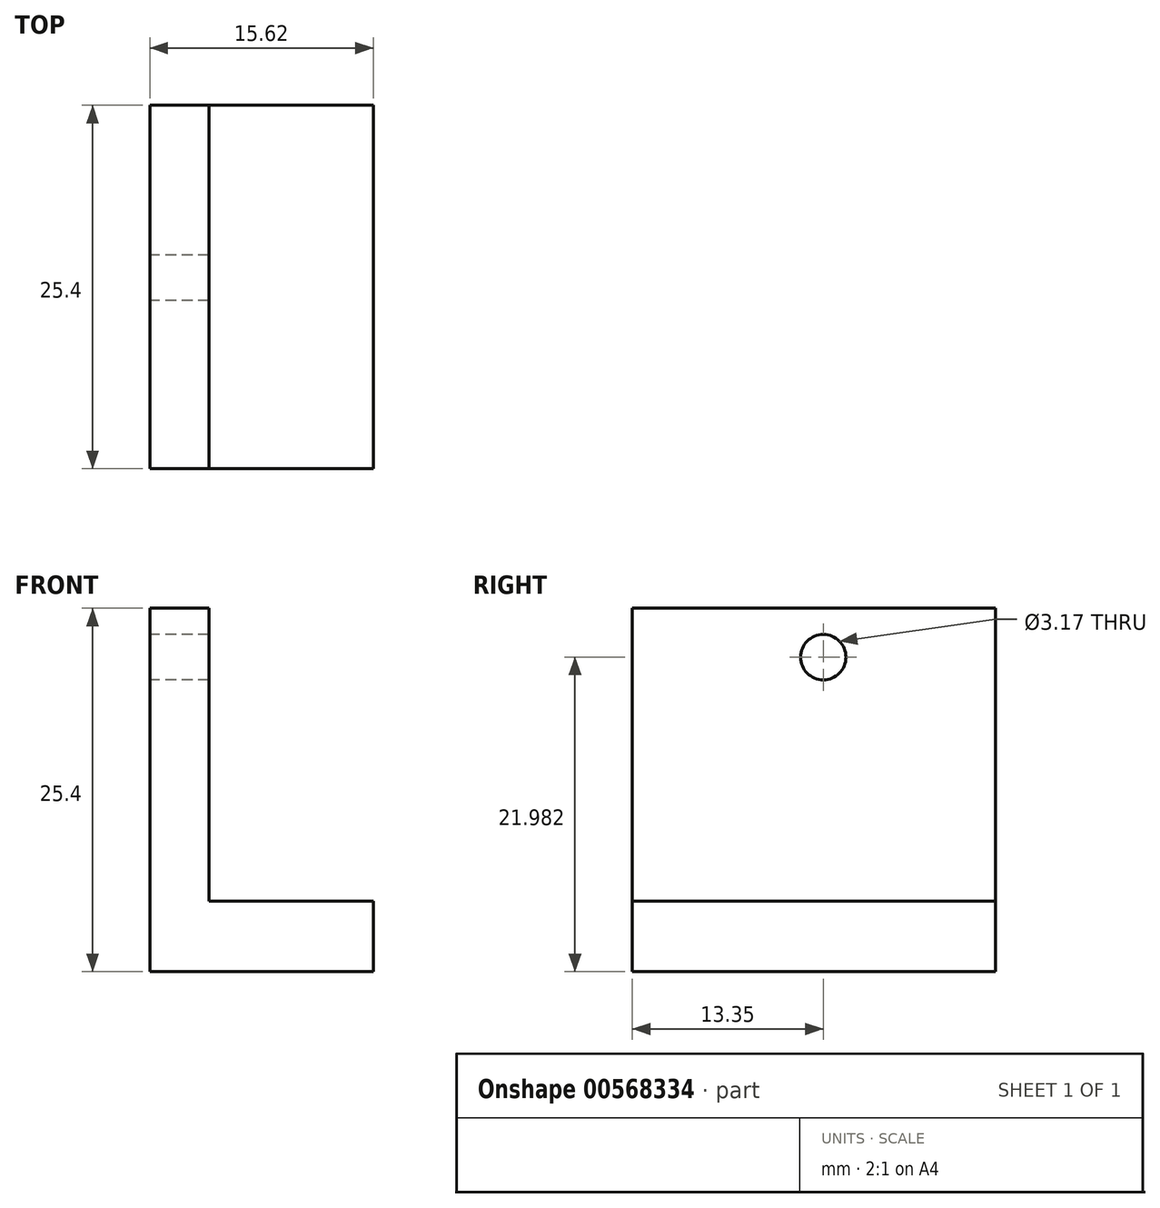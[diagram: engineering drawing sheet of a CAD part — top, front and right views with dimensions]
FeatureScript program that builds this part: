
annotation { "Feature Type Name" : "Feature", "Feature Type Description" : "" }
export const myFeature = defineFeature(function(context is Context, id is Id, definition is map)
    precondition{}
    {
        {
            var Q0;
            Q0=qCreatedBy(makeId("Front.planeOp"),FACE);
            var sketch = newSketch(context, id + "F0", { "sketchPlane" : qUnion([Q0])});
            skLineSegment(sketch, "E0.bottom", {"start": v(0, 0) * mm, "end": v(25.4, 0) * mm});
            skLineSegment(sketch, "E0.top", {"start": v(0, 25.4) * mm, "end": v(25.4, 25.4) * mm});
            skLineSegment(sketch, "E0.left", {"start": v(0, 0) * mm, "end": v(0, 25.4) * mm});
            skLineSegment(sketch, "E0.right", {"start": v(25.4, 0) * mm, "end": v(25.4, 25.4) * mm});
            skSolve(sketch);
        }
        {
            var Q0;
            Q0=makeQuery(id+"F0.imprint","IMPRINT",FACE,{"disambiguationData":[TD([[makeQuery(id+"F0.imprint","IMPRINT",EDGE,{"derivedFrom":sQuery(id+"F0.wireOp",EDGE,"E0.bottom")}),1.0]])]});
            extrude(context, id + "F1", {"entities" : qUnion([Q0]), "depth" : 25.4 * mm, "offsetDistance" : 25.4 * mm});
        }
        {
            var Q0;
            Q0=makeQuery(id+"F1.opExtrude","CAP_FACE",FACE,{"disambiguationData":[OSD([sQuery(id+"F0.wireOp",EDGE,"E0.bottom"),sQuery(id+"F0.wireOp",EDGE,"E0.top"),sQuery(id+"F0.wireOp",EDGE,"E0.left"),sQuery(id+"F0.wireOp",EDGE,"E0.right")])],"isStart":false});
            var sketch = newSketch(context, id + "F2", { "sketchPlane" : qUnion([Q0])});
            skLineSegment(sketch, "E1", {"start": v(5.04, 25.4) * mm, "end": v(5.04, 0) * mm});
            skLineSegment(sketch, "E2", {"start": v(5.04, 0) * mm, "end": v(20.66, 0) * mm});
            skLineSegment(sketch, "E3", {"start": v(20.66, 0) * mm, "end": v(20.66, 4.93) * mm});
            skLineSegment(sketch, "E4", {"start": v(20.66, 4.93) * mm, "end": v(9.18, 4.93) * mm});
            skLineSegment(sketch, "E5", {"start": v(9.18, 4.93) * mm, "end": v(9.18, 25.4) * mm});
            skSolve(sketch);
        }
        {
            var Q0;
            Q0 = qSketchRegion(id + "F2", true);
            var Q1;
            {var subQ2=sQuery(id+"F2.wireOp",EDGE,"E3");Q1=makeQuery(id+"F2.imprint","IMPRINT",FACE,{"disambiguationData":[TD([[makeQuery(id+"F2.imprint","IMPRINT",EDGE,{"derivedFrom":subQ2}),-1.0]])]});}
            var Q2;
            {var subQ0=sQuery(id+"F2.wireOp",EDGE,"E1");Q2=makeQuery(id+"F2.imprint","IMPRINT",FACE,{"disambiguationData":[TD([[makeQuery(id+"F2.imprint","IMPRINT",EDGE,{"derivedFrom":subQ0}),-1.0]])]});}
            extrude(context, id + "F3", {"entities" : qUnion([Q0, Q1, Q2]), "operationType" : NewBodyOperationType.REMOVE, "oppositeDirection" : true, "depth" : 38.1 * mm, "offsetDistance" : 25.4 * mm});
        }
        {
            var Q0;
            Q0=makeQuery(id+"F3.boolean.opBoolean","COPY",FACE,{"derivedFrom":makeQuery(id+"F3.opExtrude","SWEPT_FACE",FACE,{"disambiguationData":[OSD([sQuery(id+"F2.wireOp",EDGE,"E1")])]})});
            var sketch = newSketch(context, id + "F4", { "sketchPlane" : qUnion([Q0])});
            skCircle(sketch, "E6", {"center": v(12.05, 21.98) * mm, "radius": 1.59 * mm});
            skSolve(sketch);
        }
        {
            var Q0;
            Q0=makeQuery(id+"F4.imprint","IMPRINT",FACE,{"disambiguationData":[TD([[makeQuery(id+"F4.imprint","IMPRINT",EDGE,{"derivedFrom":sQuery(id+"F4.wireOp",EDGE,"E6")}),1.0]])]});
            extrude(context, id + "F5", {"entities" : qUnion([Q0]), "operationType" : NewBodyOperationType.REMOVE, "oppositeDirection" : true, "depth" : 12.7 * mm, "offsetDistance" : 25.4 * mm});
        }
    });
